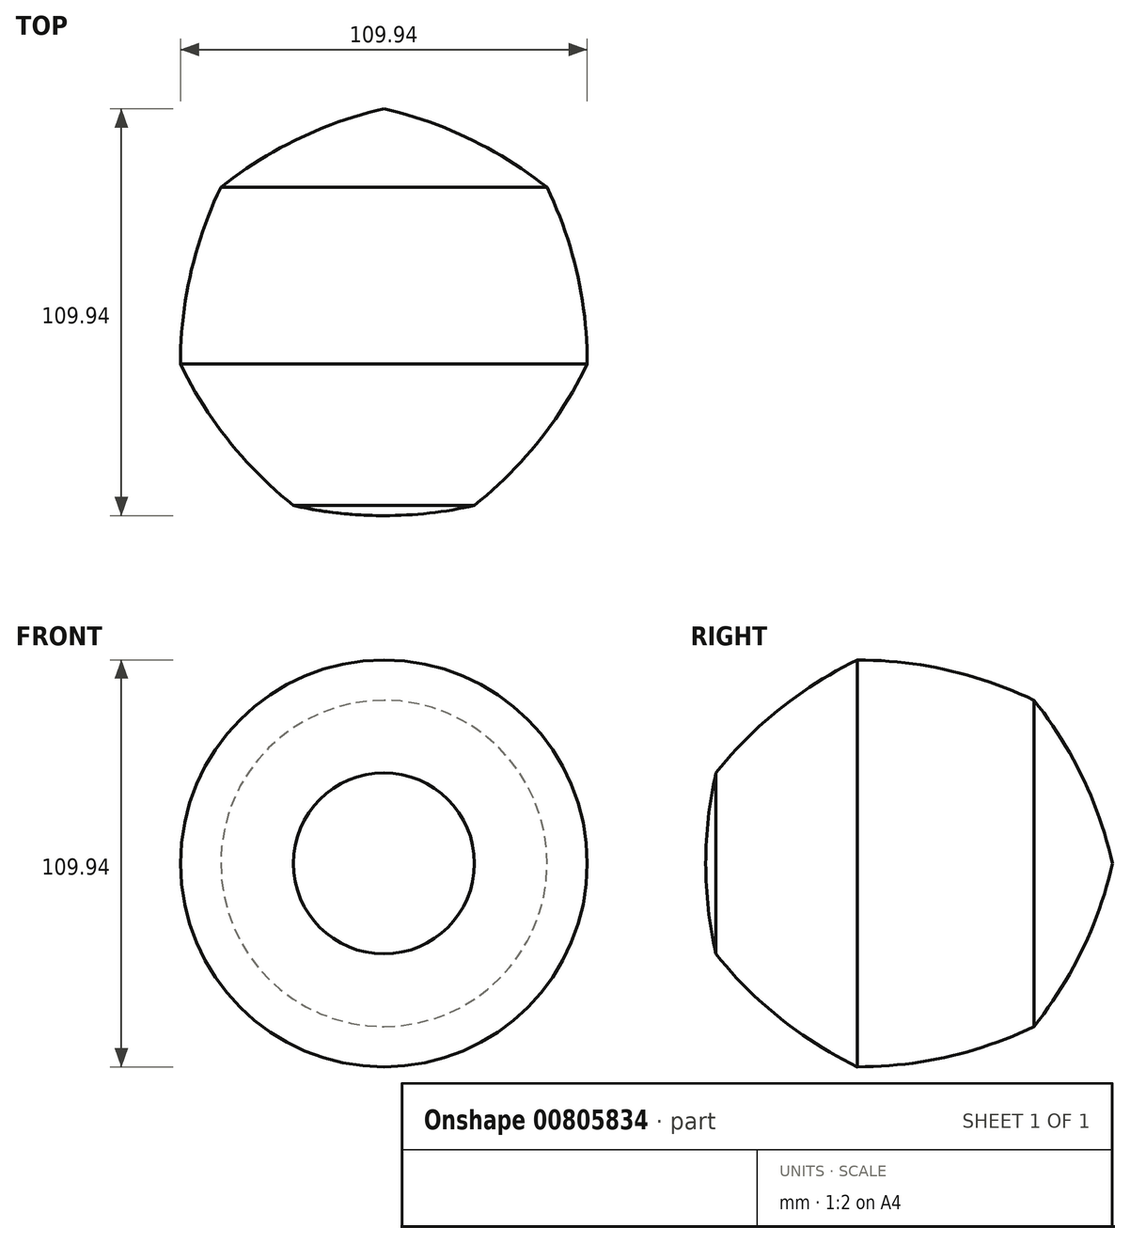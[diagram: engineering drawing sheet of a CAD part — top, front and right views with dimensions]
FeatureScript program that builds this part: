
annotation { "Feature Type Name" : "Feature", "Feature Type Description" : "" }
export const myFeature = defineFeature(function(context is Context, id is Id, definition is map)
    precondition{}
    {
        {
            var Q0;
            Q0=qCreatedBy(makeId("Top.planeOp"),FACE);
            var sketch = newSketch(context, id + "F0", { "sketchPlane" : qUnion([Q0])});
            skCircle(sketch, "E0.cCircle", {"center": v(0, 0) * mm, "radius": 50.8 * mm, "construction": true});
            skLineSegment(sketch, "E0.0", {"start": v(0, 56.38) * mm, "end": v(44.08, 35.15) * mm});
            skLineSegment(sketch, "E0.1", {"start": v(44.08, 35.15) * mm, "end": v(54.97, -12.55) * mm});
            skLineSegment(sketch, "E0.2", {"start": v(54.97, -12.55) * mm, "end": v(24.46, -50.8) * mm});
            skLineSegment(sketch, "E0.3", {"start": v(24.46, -50.8) * mm, "end": v(-24.46, -50.8) * mm});
            skLineSegment(sketch, "E0.4", {"start": v(-24.46, -50.8) * mm, "end": v(-54.97, -12.55) * mm});
            skLineSegment(sketch, "E0.5", {"start": v(-54.97, -12.55) * mm, "end": v(-44.08, 35.15) * mm});
            skLineSegment(sketch, "E0.6", {"start": v(-44.08, 35.15) * mm, "end": v(0, 56.38) * mm});
            skPoint(sketch, "E0.0.midPoint", {"position": v(22.04, 45.77) * mm});
            skCircle(sketch, "E1", {"center": v(0, 56.38) * mm, "radius": 109.94 * mm});
            skCircle(sketch, "E2", {"center": v(-44.08, 35.15) * mm, "radius": 109.94 * mm});
            skCircle(sketch, "E3", {"center": v(-54.97, -12.55) * mm, "radius": 109.94 * mm});
            skCircle(sketch, "E4", {"center": v(-24.46, -50.8) * mm, "radius": 109.94 * mm});
            skCircle(sketch, "E5", {"center": v(24.46, -50.8) * mm, "radius": 109.94 * mm});
            skCircle(sketch, "E6", {"center": v(54.97, -12.55) * mm, "radius": 109.94 * mm});
            skCircle(sketch, "E7", {"center": v(44.08, 35.15) * mm, "radius": 109.94 * mm});
            skLineSegment(sketch, "E8", {"start": v(0, 76.2) * mm, "end": v(0, -85.85) * mm});
            skSolve(sketch);
        }
        {
            var Q0;
            {var subQ1=sQuery(id+"F0.wireOp",EDGE,"E0.4");Q0=makeQuery(id+"F0.imprint","IMPRINT",FACE,{"disambiguationData":[TD([[makeQuery(id+"F0.imprint","IMPRINT",EDGE,{"derivedFrom":subQ1}),-1.0]])]});}
            var Q1;
            {var subQ0=sQuery(id+"F0.wireOp",EDGE,"E0.6");Q1=makeQuery(id+"F0.imprint","IMPRINT",FACE,{"disambiguationData":[TD([[makeQuery(id+"F0.imprint","IMPRINT",EDGE,{"derivedFrom":subQ0}),1.0]])]});}
            var Q2;
            {var subQ0=sQuery(id+"F0.wireOp",EDGE,"E0.5");Q2=makeQuery(id+"F0.imprint","IMPRINT",FACE,{"disambiguationData":[TD([[makeQuery(id+"F0.imprint","IMPRINT",EDGE,{"derivedFrom":subQ0}),1.0]])]});}
            var Q3;
            {var subQ0=sQuery(id+"F0.wireOp",EDGE,"E0.4");Q3=makeQuery(id+"F0.imprint","IMPRINT",FACE,{"disambiguationData":[TD([[makeQuery(id+"F0.imprint","IMPRINT",EDGE,{"derivedFrom":subQ0}),1.0]])]});}
            var Q4;
            {var subQ1=sQuery(id+"F0.wireOp",EDGE,"E0.3");var subQ3=sQuery(id+"F0.wireOp",EDGE,"E8");var subQ4=makeQuery(id+"F0.imprint","INTERSECT",VERTEX,{"derivedFrom":[subQ1,subQ3]});Q4=makeQuery(id+"F0.imprint","IMPRINT",FACE,{"disambiguationData":[TD([[makeQuery(id+"F0.imprint","IMPRINT",EDGE,{"disambiguationData":[TD([[subQ4,-1.0]])],"derivedFrom":subQ3}),-1.0]])]});}
            var Q5;
            Q5=sQuery(id+"F0.wireOp",EDGE,"E8");
            revolve(context, id + "F1", {"surfaceOperationType" : NewSurfaceOperationType.NEW, "entities" : qUnion([Q0, Q1, Q2, Q3, Q4]), "axis" : qUnion([Q5]), "revolveType" : RevolveType.FULL});
        }
    });
